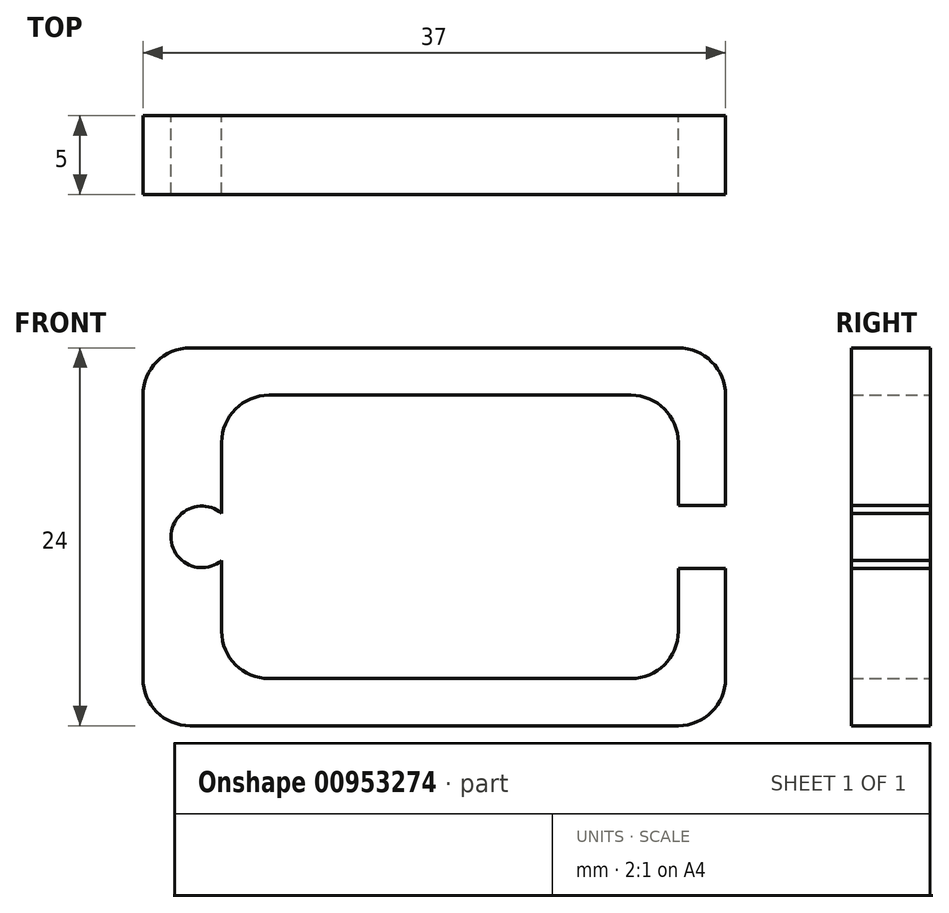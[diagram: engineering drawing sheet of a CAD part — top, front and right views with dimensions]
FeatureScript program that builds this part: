
annotation { "Feature Type Name" : "Feature", "Feature Type Description" : "" }
export const myFeature = defineFeature(function(context is Context, id is Id, definition is map)
    precondition{}
    {
        {
            var Q0;
            Q0=qCreatedBy(makeId("Front.planeOp"),FACE);
            var sketch = newSketch(context, id + "F0", { "sketchPlane" : qUnion([Q0])});
            skLineSegment(sketch, "E0.bottom", {"start": v(-18.5, 12) * mm, "end": v(18.5, 12) * mm});
            skLineSegment(sketch, "E0.top", {"start": v(-18.5, -12) * mm, "end": v(18.5, -12) * mm});
            skLineSegment(sketch, "E0.left", {"start": v(-18.5, 12) * mm, "end": v(-18.5, -12) * mm});
            skPoint(sketch, "E0.middle", {"position": v(0, 0) * mm});
            skLineSegment(sketch, "E1", {"start": v(18.5, 12) * mm, "end": v(18.5, 2) * mm});
            skLineSegment(sketch, "E2", {"start": v(15.5, 2) * mm, "end": v(15.5, 9) * mm});
            skLineSegment(sketch, "E3", {"start": v(15.5, 9) * mm, "end": v(-13.5, 9) * mm});
            skLineSegment(sketch, "E4", {"start": v(-13.5, -9) * mm, "end": v(15.5, -9) * mm});
            skLineSegment(sketch, "E5", {"start": v(15.5, -9) * mm, "end": v(15.5, -2) * mm});
            skLineSegment(sketch, "E6", {"start": v(18.5, -2) * mm, "end": v(18.5, -12) * mm});
            skLineSegment(sketch, "E7", {"start": v(-13.5, 9) * mm, "end": v(-13.5, 1.5) * mm});
            skLineSegment(sketch, "E8", {"start": v(-13.5, -9) * mm, "end": v(-13.5, -1.5) * mm});
            skArc(sketch, "E9", {"start": v(-13.5, 1.5) * mm, "mid": v(-16.71, 0) * mm, "end": v(-13.5, -1.5) * mm});
            skLineSegment(sketch, "E10", {"start": v(18.5, 2) * mm, "end": v(15.5, 2) * mm});
            skLineSegment(sketch, "E11", {"start": v(18.5, -2) * mm, "end": v(15.5, -2) * mm});
            skSolve(sketch);
        }
        {
            var Q0;
            Q0=makeQuery(id+"F0.imprint","IMPRINT",FACE,{"disambiguationData":[TD([[makeQuery(id+"F0.imprint","IMPRINT",EDGE,{"derivedFrom":sQuery(id+"F0.wireOp",EDGE,"E0.bottom")}),-1.0]])]});
            extrude(context, id + "F1", {"entities" : qUnion([Q0]), "endBound" : BoundingType.SYMMETRIC, "depth" : 5 * mm, "offsetDistance" : 25 * mm});
        }
        {
            var Q0;
            Q0=makeQuery(id+"F1.opExtrude","SWEPT_EDGE",EDGE,{"disambiguationData":[OSD([sQuery(id+"F0.wireOp",EDGE,"E0.bottom"),sQuery(id+"F0.wireOp",EDGE,"E1")])]});
            var Q1;
            Q1=makeQuery(id+"F1.opExtrude","SWEPT_EDGE",EDGE,{"disambiguationData":[OSD([sQuery(id+"F0.wireOp",EDGE,"E0.top"),sQuery(id+"F0.wireOp",EDGE,"E6")])]});
            var Q2;
            Q2=makeQuery(id+"F1.opExtrude","SWEPT_EDGE",EDGE,{"disambiguationData":[OSD([sQuery(id+"F0.wireOp",EDGE,"E0.bottom"),sQuery(id+"F0.wireOp",EDGE,"E0.left")])]});
            var Q3;
            Q3=makeQuery(id+"F1.opExtrude","SWEPT_EDGE",EDGE,{"disambiguationData":[OSD([sQuery(id+"F0.wireOp",EDGE,"E0.top"),sQuery(id+"F0.wireOp",EDGE,"E0.left")])]});
            var Q4;
            Q4=makeQuery(id+"F1.opExtrude","SWEPT_EDGE",EDGE,{"disambiguationData":[OSD([sQuery(id+"F0.wireOp",EDGE,"E4"),sQuery(id+"F0.wireOp",EDGE,"E5")])]});
            var Q5;
            Q5=makeQuery(id+"F1.opExtrude","SWEPT_EDGE",EDGE,{"disambiguationData":[OSD([sQuery(id+"F0.wireOp",EDGE,"E2"),sQuery(id+"F0.wireOp",EDGE,"E3")])]});
            var Q6;
            Q6=makeQuery(id+"F1.opExtrude","SWEPT_EDGE",EDGE,{"disambiguationData":[OSD([sQuery(id+"F0.wireOp",EDGE,"E3"),sQuery(id+"F0.wireOp",EDGE,"E7")])]});
            var Q7;
            Q7=makeQuery(id+"F1.opExtrude","SWEPT_EDGE",EDGE,{"disambiguationData":[OSD([sQuery(id+"F0.wireOp",EDGE,"E4"),sQuery(id+"F0.wireOp",EDGE,"E8")])]});
            fillet(context, id + "F2", {"entities" : qUnion([Q0, Q1, Q2, Q3, Q4, Q5, Q6, Q7]), "radius" : 3 * mm, "tangentPropagation" : true, "allowEdgeOverflow" : false});
        }
    });
